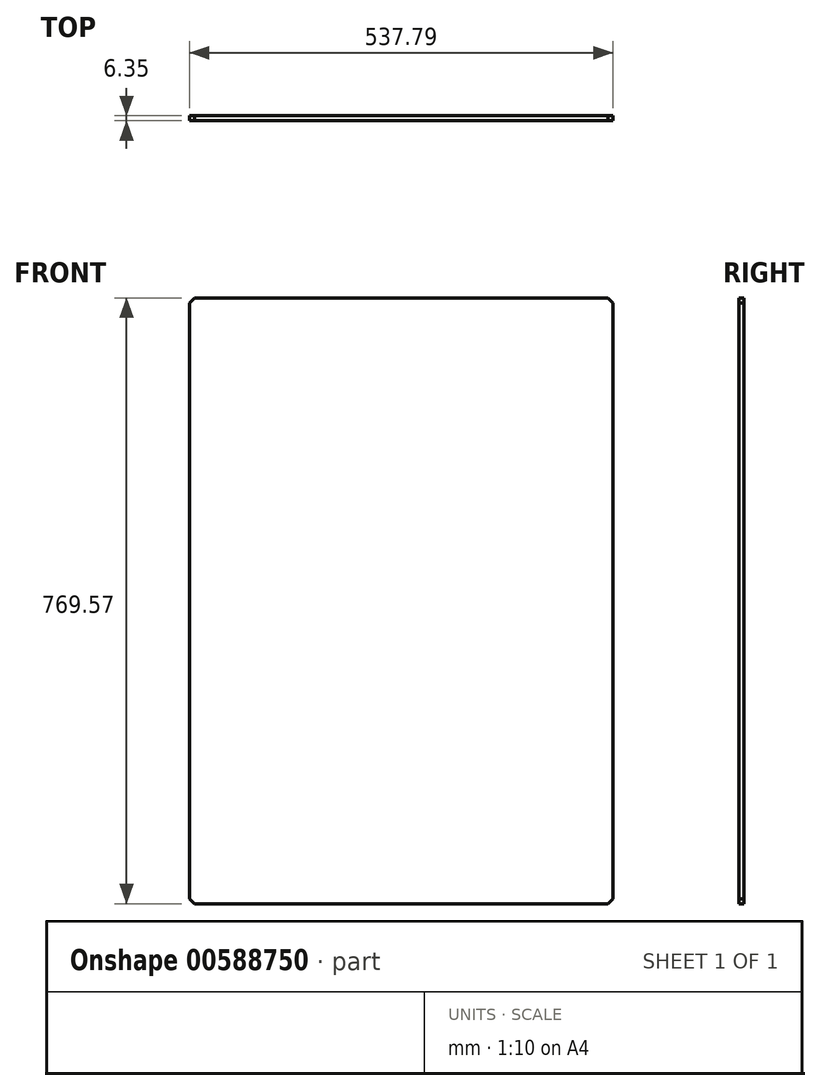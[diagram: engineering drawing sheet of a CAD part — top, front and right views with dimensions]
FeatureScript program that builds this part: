
annotation { "Feature Type Name" : "Feature", "Feature Type Description" : "" }
export const myFeature = defineFeature(function(context is Context, id is Id, definition is map)
    precondition{}
    {
        {
            var Q0;
            Q0=qCreatedBy(makeId("Front.planeOp"),FACE);
            var sketch = newSketch(context, id + "F0", { "sketchPlane" : qUnion([Q0])});
            skLineSegment(sketch, "E0.bottom", {"start": v(0, 0) * mm, "end": v(537.8, 0) * mm});
            skLineSegment(sketch, "E0.top", {"start": v(0, -769.57) * mm, "end": v(537.8, -769.57) * mm});
            skLineSegment(sketch, "E0.left", {"start": v(0, 0) * mm, "end": v(0, -769.57) * mm});
            skLineSegment(sketch, "E0.right", {"start": v(537.8, 0) * mm, "end": v(537.8, -769.57) * mm});
            skSolve(sketch);
        }
        {
            var Q0;
            Q0=makeQuery(id+"F0.imprint","IMPRINT",FACE,{"disambiguationData":[TD([[makeQuery(id+"F0.imprint","IMPRINT",EDGE,{"derivedFrom":sQuery(id+"F0.wireOp",EDGE,"E0.bottom")}),-1.0]])]});
            extrude(context, id + "F1", {"entities" : qUnion([Q0]), "depth" : 6.35 * mm, "offsetDistance" : 25.4 * mm});
        }
        {
            var Q0;
            Q0=makeQuery(id+"F1.opExtrude","SWEPT_EDGE",EDGE,{"disambiguationData":[OSD([sQuery(id+"F0.wireOp",EDGE,"E0.bottom"),sQuery(id+"F0.wireOp",EDGE,"E0.left")])]});
            var Q1;
            Q1=makeQuery(id+"F1.opExtrude","SWEPT_EDGE",EDGE,{"disambiguationData":[OSD([sQuery(id+"F0.wireOp",EDGE,"E0.bottom"),sQuery(id+"F0.wireOp",EDGE,"E0.right")])]});
            var Q2;
            Q2=makeQuery(id+"F1.opExtrude","SWEPT_EDGE",EDGE,{"disambiguationData":[OSD([sQuery(id+"F0.wireOp",EDGE,"E0.top"),sQuery(id+"F0.wireOp",EDGE,"E0.right")])]});
            var Q3;
            Q3=makeQuery(id+"F1.opExtrude","SWEPT_EDGE",EDGE,{"disambiguationData":[OSD([sQuery(id+"F0.wireOp",EDGE,"E0.top"),sQuery(id+"F0.wireOp",EDGE,"E0.left")])]});
            chamfer(context, id + "F2", {"entities" : qUnion([Q0, Q1, Q2, Q3]), "width" : 6.35 * mm, "tangentPropagation" : true});
        }
    });
